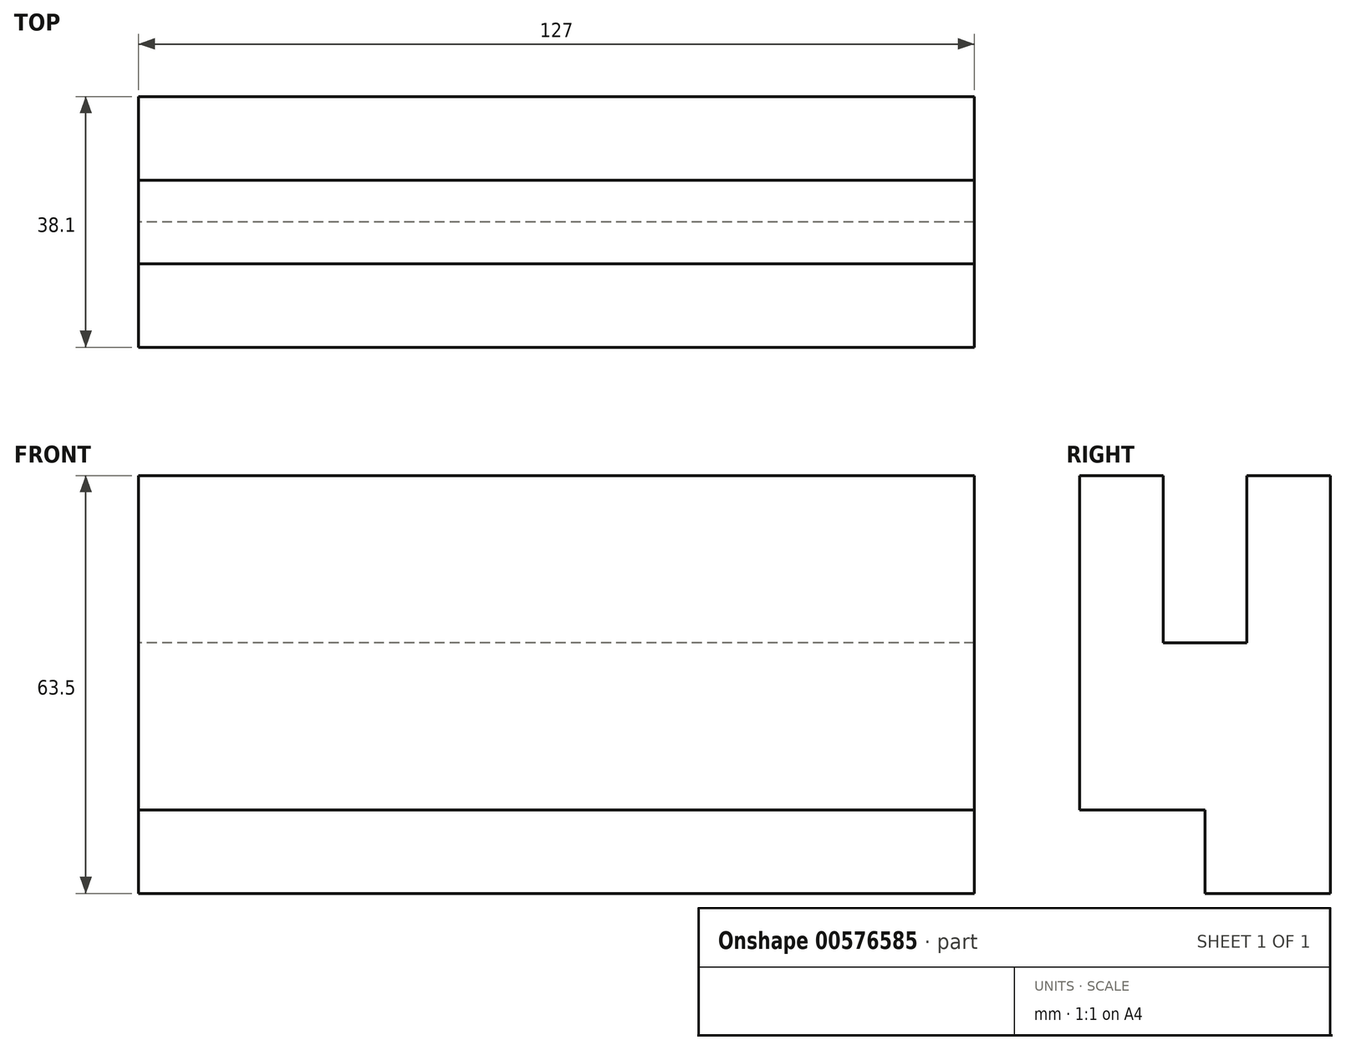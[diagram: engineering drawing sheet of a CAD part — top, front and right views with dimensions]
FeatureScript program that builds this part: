
annotation { "Feature Type Name" : "Feature", "Feature Type Description" : "" }
export const myFeature = defineFeature(function(context is Context, id is Id, definition is map)
    precondition{}
    {
        {
            var Q0;
            Q0=qCreatedBy(makeId("Right.planeOp"),FACE);
            var sketch = newSketch(context, id + "F0", { "sketchPlane" : qUnion([Q0])});
            skLineSegment(sketch, "E0", {"start": v(0, 36.45) * mm, "end": v(12.7, 36.45) * mm});
            skLineSegment(sketch, "E1", {"start": v(12.7, 36.45) * mm, "end": v(12.7, 11.05) * mm});
            skLineSegment(sketch, "E2", {"start": v(12.7, 11.05) * mm, "end": v(25.4, 11.05) * mm});
            skLineSegment(sketch, "E3", {"start": v(25.4, 11.05) * mm, "end": v(25.4, 36.45) * mm});
            skLineSegment(sketch, "E4", {"start": v(25.4, 36.45) * mm, "end": v(38.1, 36.45) * mm});
            skLineSegment(sketch, "E5", {"start": v(38.1, 36.45) * mm, "end": v(38.1, -27.05) * mm});
            skLineSegment(sketch, "E6", {"start": v(38.1, -27.05) * mm, "end": v(19.05, -27.05) * mm});
            skLineSegment(sketch, "E7", {"start": v(19.05, -27.05) * mm, "end": v(19.05, -14.35) * mm});
            skLineSegment(sketch, "E8", {"start": v(19.05, -14.35) * mm, "end": v(0, -14.35) * mm});
            skLineSegment(sketch, "E9", {"start": v(0, 36.45) * mm, "end": v(0, -14.35) * mm});
            skSolve(sketch);
        }
        {
            var Q0;
            Q0 = qSketchRegion(id + "F0", true);
            extrude(context, id + "F1", {"entities" : qUnion([Q0]), "depth" : 127 * mm, "offsetDistance" : 25.4 * mm});
        }
    });
